# Revit family: 1HVAC_Ductwork_Airzone_Supply-Grille_RTHV
name_source: partatom
category: Air Terminals
revit_build: Autodesk Revit 2016 (Build: 20161004_0715(x64)
units: mm (PartAtom-declared; Revit-internal decimal feet)

## family parameters
Always vertical = Yes
Cut with Voids When Loaded = No
OmniClass Number = 23.75.70.21.27.11
OmniClass Title = Diffusers, Registers, and Grilles
Part Type = Normal
Room Calculation Point = Yes
Round Connector Dimension = Use Diameter
Shared = No
Work Plane-Based = No

## types (1)
- INVALID TYPE - Use Load Family and Type Catalog instead
    Accessories Material = Metal - AIRZONE - Extruded Aluminium - Anodized (Matt Silver Color)
    Ak = 2.53
    Compatible Accesories = Mounting frame. Plenum for grille (PREJ)
    Description = Supply grille of horizontal-vertical double deflection with air flow regulation incorporated
    Disclaimer = All information provided in this model is reviewed before being published. However, Airzone cannot guarantee this model is error-free, therefore users are strongly encouraged to check for technical documentation and updates
    Duct Height = 150 mm
    Duct Width = 300 mm
    Effective Area = 253.00 cm²
    Finish = White (RAL 9010)
    Fixing = Clip (K), mounting frame required. Screw (T), mounting frame required
    Grille Material = Metal - AIRZONE - Grille 20 mm - White (RAL 9010)
    Long Description = Extruded aluminum grille supply. 26-mm standard frame. Horizontal and vertical moving slats for an individual regulation as they adapt the air range and the air stream to the needs of the zone. Integrated flow regulation damper, manually operable by screw.
    Main Material = Metal - AIRZONE - Extruded Aluminium - White (RAL 9010)
    Manufacturer = AIRZONE
    Max Flow = 1500 m³/h
    Min Flow = 150 m³/h
    Model = INVALID – Type not loaded via type catalog
    Product Code = INVALID – Type not loaded via type catalog
    Product Comments = Refer to technical documentation for further details
    Product Documentation Download URL = http://doc.airzone.es
    Revit Model Version = 1.0
    Type Image Comments = Image available in product documentation download
    URL = www.airzone.es
    c1 = 0.000525
    c2 = -2.051
    c3 = -98.8
    c4 = -62.63
    c5 = 53.01
    c6 = 4.8467
    c7 = 0.02882
    c8 = -0.4791

## geometry (parser evidence)
native form markers: Sweep x2
no freeform markers — native parametric forms only
